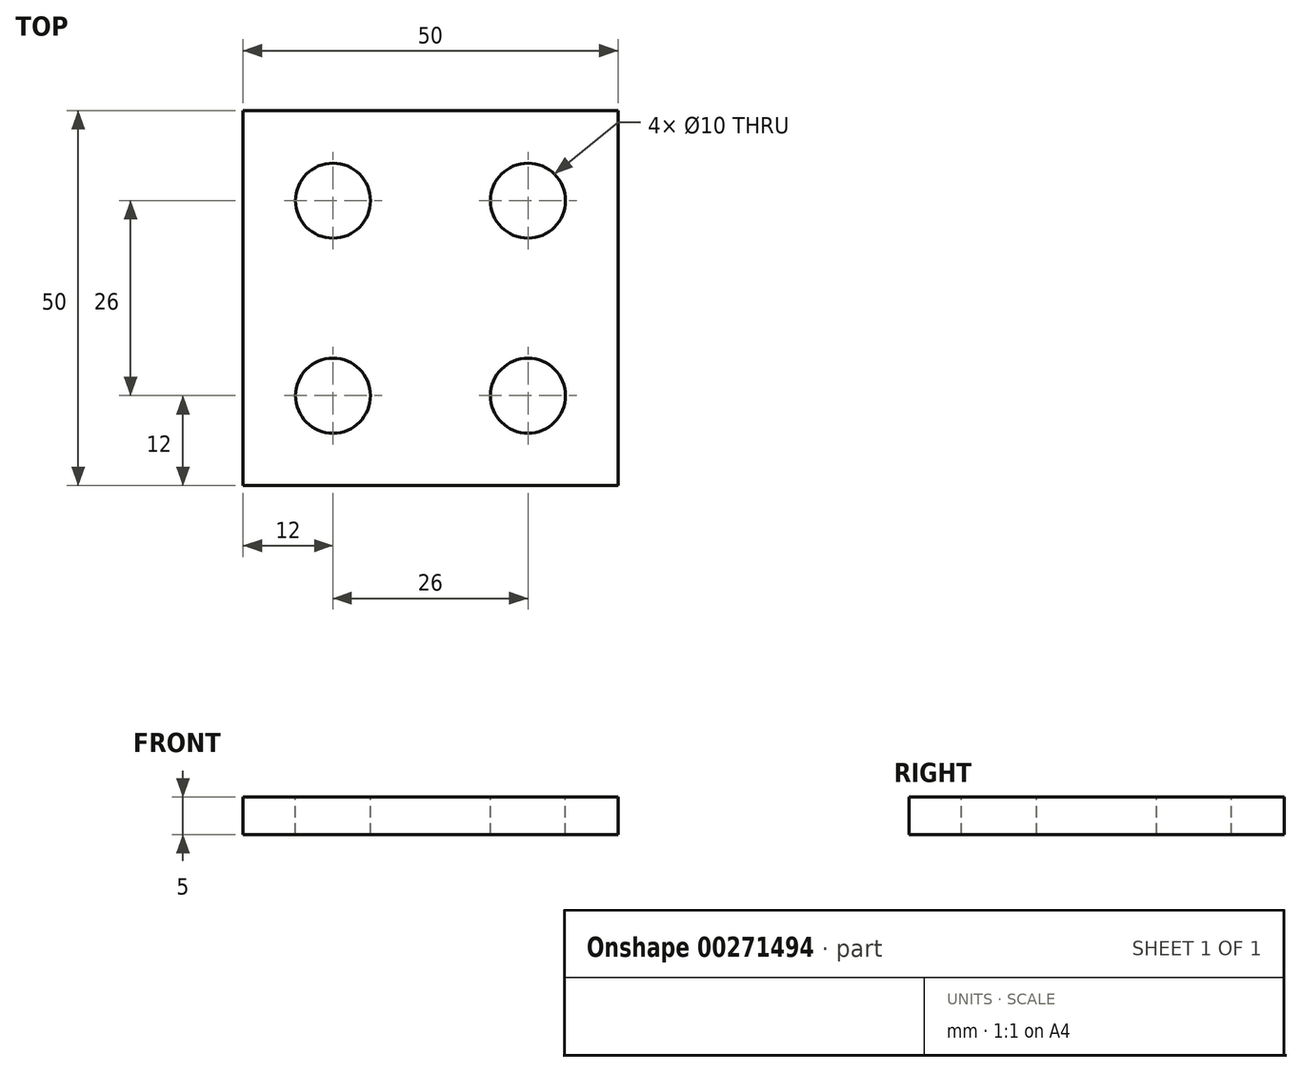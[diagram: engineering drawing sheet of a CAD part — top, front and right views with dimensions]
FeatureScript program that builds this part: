
annotation { "Feature Type Name" : "Feature", "Feature Type Description" : "" }
export const myFeature = defineFeature(function(context is Context, id is Id, definition is map)
    precondition{}
    {
        {
            var Q0;
            Q0=qCreatedBy(makeId("Top.planeOp"),FACE);
            var sketch = newSketch(context, id + "F0", { "sketchPlane" : qUnion([Q0])});
            skLineSegment(sketch, "E0.bottom", {"start": v(-25, 25) * mm, "end": v(25, 25) * mm});
            skLineSegment(sketch, "E0.top", {"start": v(-25, -25) * mm, "end": v(25, -25) * mm});
            skLineSegment(sketch, "E0.left", {"start": v(-25, 25) * mm, "end": v(-25, -25) * mm});
            skLineSegment(sketch, "E0.right", {"start": v(25, 25) * mm, "end": v(25, -25) * mm});
            skPoint(sketch, "E0.middle", {"position": v(0, 0) * mm});
            skSolve(sketch);
        }
        {
            var Q0;
            Q0=makeQuery(id+"F0.imprint","IMPRINT",FACE,{"disambiguationData":[TD([[makeQuery(id+"F0.imprint","IMPRINT",EDGE,{"derivedFrom":sQuery(id+"F0.wireOp",EDGE,"E0.bottom")}),-1.0]])]});
            extrude(context, id + "F1", {"entities" : qUnion([Q0]), "depth" : 5 * mm});
        }
        {
            var Q0;
            Q0=makeQuery(id+"F1.opExtrude","CAP_FACE",FACE,{"disambiguationData":[OSD([sQuery(id+"F0.wireOp",EDGE,"E0.bottom"),sQuery(id+"F0.wireOp",EDGE,"E0.top"),sQuery(id+"F0.wireOp",EDGE,"E0.left"),sQuery(id+"F0.wireOp",EDGE,"E0.right")])],"isStart":false});
            var sketch = newSketch(context, id + "F2", { "sketchPlane" : qUnion([Q0])});
            skPoint(sketch, "E1", {"position": v(0, 9.92) * mm});
            skSolve(sketch);
        }
        {
            var Q0;
            Q0=makeQuery(id+"F2.imprint","IMPRINT",FACE,{"disambiguationData":[TD([[makeQuery(id+"F2.imprint","IMPRINT",EDGE,{"derivedFrom":makeQuery(id+"F1.opExtrude","CAP_EDGE",EDGE,{"disambiguationData":[OSD([sQuery(id+"F0.wireOp",EDGE,"E0.bottom")])],"isStart":false})}),-1.0]])]});
            var sketch = newSketch(context, id + "F3", { "sketchPlane" : qUnion([Q0])});
            skPoint(sketch, "E2", {"position": v(-13, 13) * mm});
            skLineSegment(sketch, "E3.0.0", {"start": v(25, 25) * mm, "end": v(-25, 25) * mm});
            skLineSegment(sketch, "E3.0.1", {"start": v(-25, 25) * mm, "end": v(-25, -25) * mm});
            skLineSegment(sketch, "E3.0.2", {"start": v(-25, -25) * mm, "end": v(25, -25) * mm});
            skLineSegment(sketch, "E3.0.3", {"start": v(25, -25) * mm, "end": v(25, 25) * mm});
            skLineSegment(sketch, "E4", {"start": v(-25, 0) * mm, "end": v(25, 0) * mm, "construction": true});
            skLineSegment(sketch, "E5", {"start": v(0, 25) * mm, "end": v(0, -25) * mm, "construction": true});
            skPoint(sketch, "E6.MirrorP", {"position": v(13, 13) * mm});
            skPoint(sketch, "E7.MirrorP", {"position": v(-13, -13) * mm});
            skPoint(sketch, "E8.MirrorP", {"position": v(13, -13) * mm});
            skSolve(sketch);
        }
        {
            var Q0;
            Q0=sQuery(id+"F3.wireOp",VERTEX,"E2");
            var Q1;
            Q1=sQuery(id+"F3.wireOp",VERTEX,"E6.MirrorP");
            var Q2;
            Q2=sQuery(id+"F3.wireOp",VERTEX,"E8.MirrorP");
            var Q3;
            Q3=sQuery(id+"F3.wireOp",VERTEX,"E7.MirrorP");
            var Q4;
            Q4=makeQuery(id+"F1.opExtrude","SWEPT_BODY",BODY,{"disambiguationData":[OSD([sQuery(id+"F0.wireOp",EDGE,"E0.bottom"),sQuery(id+"F0.wireOp",EDGE,"E0.top"),sQuery(id+"F0.wireOp",EDGE,"E0.left"),sQuery(id+"F0.wireOp",EDGE,"E0.right")])]});
            hole(context, id + "F4", {"style" : HoleStyle.SIMPLE, "endStyle" : HoleEndStyle.THROUGH, "holeDiameter" : 10 * mm, "tappedDepth" : 12 * mm, "tapClearance" : 3, "locations" : qUnion([Q0, Q1, Q2, Q3]), "scope" : qUnion([Q4])});
        }
    });
